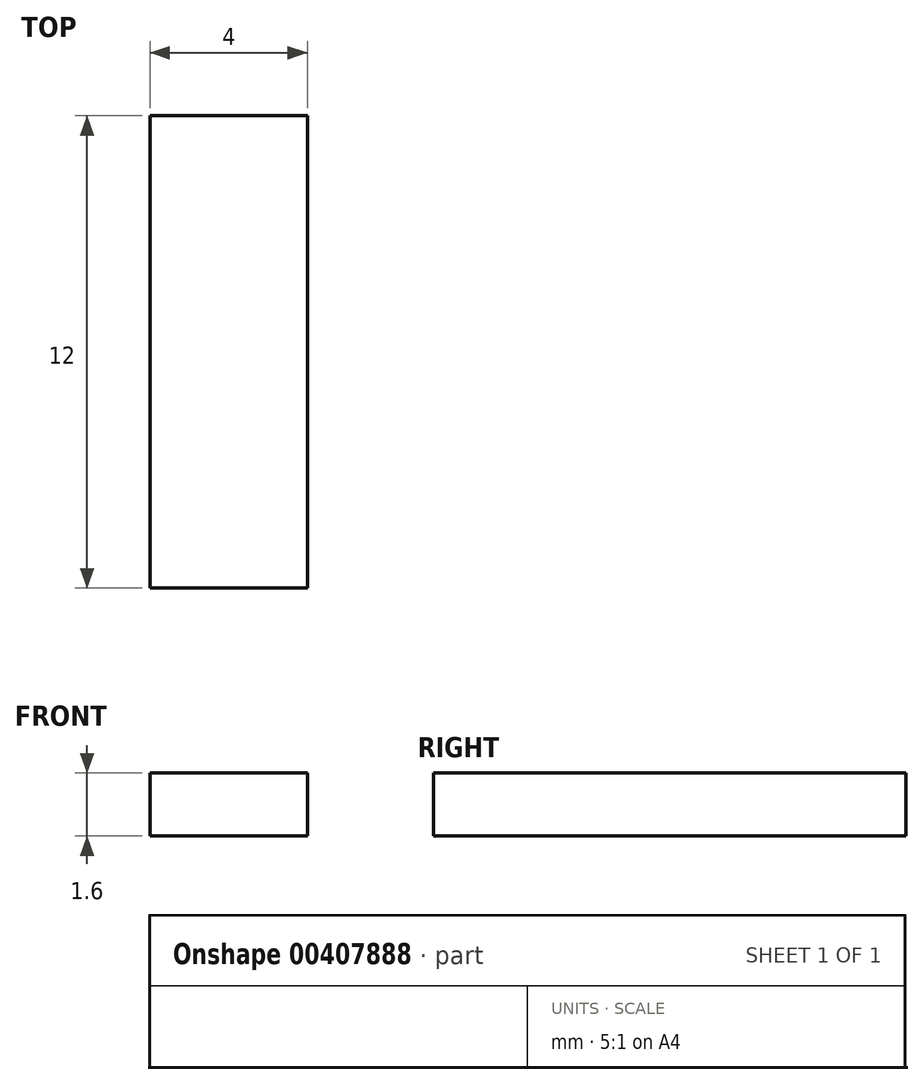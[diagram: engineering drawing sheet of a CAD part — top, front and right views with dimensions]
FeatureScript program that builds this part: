
annotation { "Feature Type Name" : "Feature", "Feature Type Description" : "" }
export const myFeature = defineFeature(function(context is Context, id is Id, definition is map)
    precondition{}
    {
        {
            var Q0;
            Q0=qCreatedBy(makeId("Front.planeOp"),FACE);
            var sketch = newSketch(context, id + "F0", { "sketchPlane" : qUnion([Q0])});
            skLineSegment(sketch, "E0.bottom", {"start": v(0, 0) * mm, "end": v(4, 0) * mm});
            skLineSegment(sketch, "E0.top", {"start": v(0, 1.6) * mm, "end": v(4, 1.6) * mm});
            skLineSegment(sketch, "E0.left", {"start": v(0, 0) * mm, "end": v(0, 1.6) * mm});
            skLineSegment(sketch, "E0.right", {"start": v(4, 0) * mm, "end": v(4, 1.6) * mm});
            skSolve(sketch);
        }
        {
            var Q0;
            Q0=makeQuery(id+"F0.imprint","IMPRINT",FACE,{"disambiguationData":[TD([[makeQuery(id+"F0.imprint","IMPRINT",EDGE,{"derivedFrom":sQuery(id+"F0.wireOp",EDGE,"E0.bottom")}),1.0]])]});
            extrude(context, id + "F1", {"entities" : qUnion([Q0]), "depth" : 12 * mm});
        }
    });
